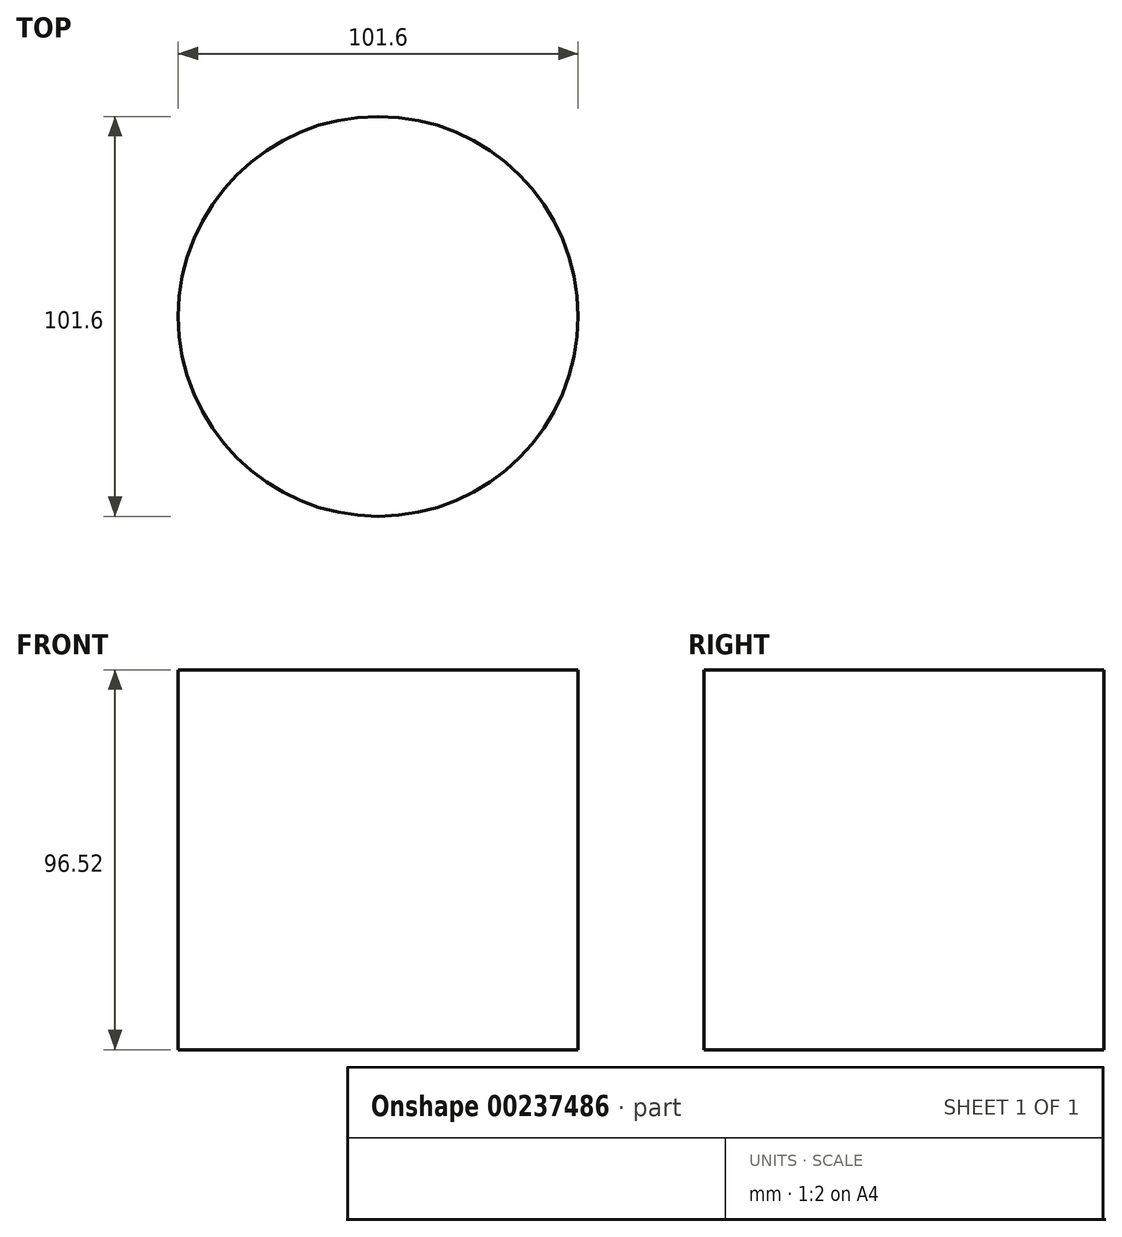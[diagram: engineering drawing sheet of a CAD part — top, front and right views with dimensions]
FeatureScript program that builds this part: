
annotation { "Feature Type Name" : "Feature", "Feature Type Description" : "" }
export const myFeature = defineFeature(function(context is Context, id is Id, definition is map)
    precondition{}
    {
        {
            var Q0;
            Q0=qCreatedBy(makeId("Top.planeOp"),FACE);
            var sketch = newSketch(context, id + "F0", { "sketchPlane" : qUnion([Q0])});
            skCircle(sketch, "E0", {"center": v(0, 0) * mm, "radius": 50.8 * mm});
            skSolve(sketch);
        }
        {
            var Q0;
            Q0=makeQuery(id+"F0.imprint","IMPRINT",FACE,{"disambiguationData":[TD([[makeQuery(id+"F0.imprint","IMPRINT",EDGE,{"derivedFrom":sQuery(id+"F0.wireOp",EDGE,"E0")}),1.0]])]});
            extrude(context, id + "F1", {"entities" : qUnion([Q0]), "depth" : 96.52 * mm});
        }
    });
